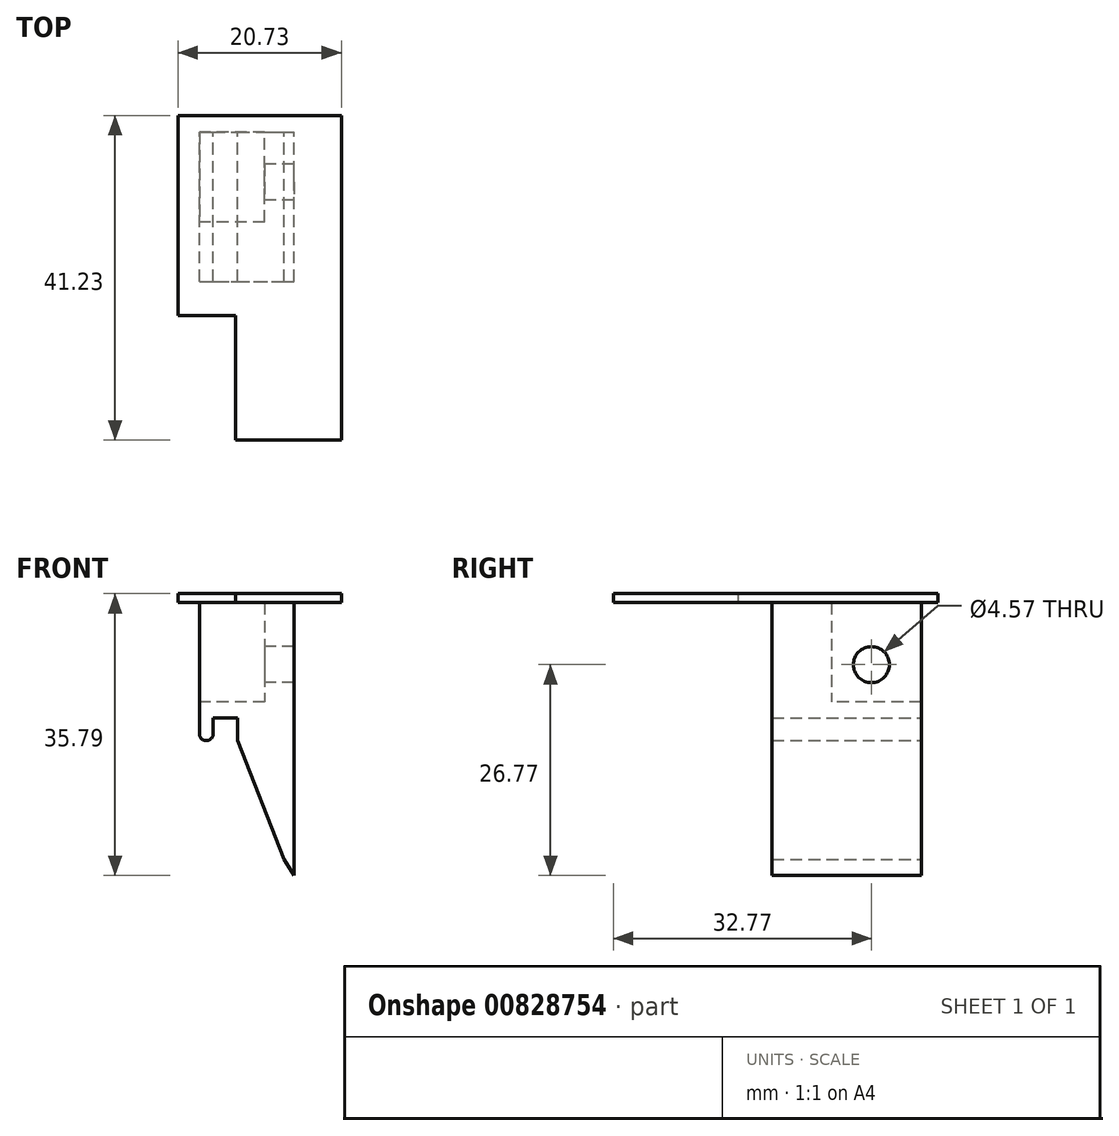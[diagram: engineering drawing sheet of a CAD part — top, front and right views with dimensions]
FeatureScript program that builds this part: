
annotation { "Feature Type Name" : "Feature", "Feature Type Description" : "" }
export const myFeature = defineFeature(function(context is Context, id is Id, definition is map)
    precondition{}
    {
        {
            var Q0;
            Q0=qCreatedBy(makeId("Front.planeOp"),FACE);
            var sketch = newSketch(context, id + "F0", { "sketchPlane" : qUnion([Q0])});
            skLineSegment(sketch, "E0", {"start": v(-12.01, 26.3) * mm, "end": v(-12.01, 8.78) * mm});
            skLineSegment(sketch, "E1", {"start": v(-12.01, 8.78) * mm, "end": v(-10.26, 8.78) * mm});
            skLineSegment(sketch, "E2", {"start": v(-10.26, 8.78) * mm, "end": v(-10.26, 11.67) * mm});
            skLineSegment(sketch, "E3", {"start": v(-10.26, 11.67) * mm, "end": v(-7.14, 11.67) * mm});
            skLineSegment(sketch, "E4", {"start": v(-7.14, 11.67) * mm, "end": v(-7.14, 8.78) * mm});
            skLineSegment(sketch, "E5", {"start": v(-12.01, 26.3) * mm, "end": v(0, 26.3) * mm});
            skLineSegment(sketch, "E6", {"start": v(0, 26.3) * mm, "end": v(0, -8.34) * mm});
            skLineSegment(sketch, "E7", {"start": v(-7.14, 8.78) * mm, "end": v(-1.25, -6.3) * mm});
            skLineSegment(sketch, "E8", {"start": v(-1.25, -6.3) * mm, "end": v(0, -8.34) * mm});
            skSolve(sketch);
        }
        {
            var Q0;
            Q0=makeQuery(id+"F0.imprint","IMPRINT",FACE,{"disambiguationData":[TD([[makeQuery(id+"F0.imprint","IMPRINT",EDGE,{"derivedFrom":sQuery(id+"F0.wireOp",EDGE,"E0")}),1.0]])]});
            extrude(context, id + "F1", {"entities" : qUnion([Q0]), "depth" : 18.95 * mm, "offsetDistance" : 25.4 * mm});
        }
        {
            var Q0;
            Q0=makeQuery(id+"F1.opExtrude","SWEPT_FACE",FACE,{"disambiguationData":[OSD([sQuery(id+"F0.wireOp",EDGE,"E5")])]});
            var sketch = newSketch(context, id + "F2", { "sketchPlane" : qUnion([Q0])});
            skLineSegment(sketch, "E9", {"start": v(-14.7, 2.1) * mm, "end": v(6.02, 2.1) * mm});
            skLineSegment(sketch, "E10", {"start": v(6.02, 2.1) * mm, "end": v(6.02, -39.12) * mm});
            skLineSegment(sketch, "E11", {"start": v(6.02, -39.12) * mm, "end": v(-7.41, -39.12) * mm});
            skLineSegment(sketch, "E12", {"start": v(-7.41, -39.12) * mm, "end": v(-7.41, -23.3) * mm});
            skLineSegment(sketch, "E13", {"start": v(-7.41, -23.3) * mm, "end": v(-14.7, -23.3) * mm});
            skLineSegment(sketch, "E14", {"start": v(-14.7, -23.3) * mm, "end": v(-14.7, 2.1) * mm});
            skSolve(sketch);
        }
        {
            var Q0;
            Q0=qSketchRegion(id+"F2",true);
            extrude(context, id + "F3", {"entities" : qUnion([Q0]), "operationType" : NewBodyOperationType.ADD, "depth" : 1.14 * mm, "offsetDistance" : 25.4 * mm});
        }
        {
            var Q0;
            Q0=makeQuery(id+"F1.opExtrude","SWEPT_EDGE",EDGE,{"disambiguationData":[OSD([sQuery(id+"F0.wireOp",EDGE,"E0"),sQuery(id+"F0.wireOp",EDGE,"E1")])]});
            var Q1;
            Q1=makeQuery(id+"F1.opExtrude","SWEPT_EDGE",EDGE,{"disambiguationData":[OSD([sQuery(id+"F0.wireOp",EDGE,"E1"),sQuery(id+"F0.wireOp",EDGE,"E2")])]});
            fillet(context, id + "F4", {"entities" : qUnion([Q0, Q1]), "radius" : 0.84 * mm, "tangentPropagation" : true, "allowEdgeOverflow" : false});
        }
        {
            var Q0;
            Q0=makeQuery(id+"F1.opExtrude","SWEPT_FACE",FACE,{"disambiguationData":[OSD([sQuery(id+"F0.wireOp",EDGE,"E0")])]});
            var sketch = newSketch(context, id + "F5", { "sketchPlane" : qUnion([Q0])});
            skLineSegment(sketch, "E15.bottom", {"start": v(0, 26.3) * mm, "end": v(11.43, 26.3) * mm});
            skLineSegment(sketch, "E15.top", {"start": v(0, 13.7) * mm, "end": v(11.43, 13.7) * mm});
            skLineSegment(sketch, "E15.left", {"start": v(0, 26.3) * mm, "end": v(0, 13.7) * mm});
            skLineSegment(sketch, "E15.right", {"start": v(11.43, 26.3) * mm, "end": v(11.43, 13.7) * mm});
            skPoint(sketch, "E16", {"position": v(6.17, 18.35) * mm});
            skSolve(sketch);
        }
        {
            var Q0;
            Q0=qSketchRegion(id+"F5",true);
            extrude(context, id + "F6", {"entities" : qUnion([Q0]), "operationType" : NewBodyOperationType.REMOVE, "oppositeDirection" : true, "depth" : 8.3 * mm, "offsetDistance" : 25.4 * mm});
        }
        {
            var Q0;
            Q0=makeQuery(id+"F6.boolean.opBoolean","COPY",FACE,{"derivedFrom":makeQuery(id+"F6.opExtrude","CAP_FACE",FACE,{"disambiguationData":[OSD([sQuery(id+"F5.wireOp",EDGE,"E15.bottom"),sQuery(id+"F5.wireOp",EDGE,"E15.top"),sQuery(id+"F5.wireOp",EDGE,"E15.left"),sQuery(id+"F5.wireOp",EDGE,"E15.right")])],"isStart":false})});
            var sketch = newSketch(context, id + "F7", { "sketchPlane" : qUnion([Q0])});
            skLineSegment(sketch, "E17.bottom", {"start": v(0, 26.3) * mm, "end": v(11.43, 26.3) * mm});
            skLineSegment(sketch, "E17.top", {"start": v(0, 13.7) * mm, "end": v(11.43, 13.7) * mm});
            skLineSegment(sketch, "E17.left", {"start": v(0, 26.3) * mm, "end": v(0, 13.7) * mm});
            skLineSegment(sketch, "E17.right", {"start": v(11.43, 26.3) * mm, "end": v(11.43, 13.7) * mm});
            skPoint(sketch, "E18", {"position": v(6.35, 18.43) * mm});
            skSolve(sketch);
        }
        {
            var Q0;
            Q0=sQuery(id+"F7.wireOp",VERTEX,"E18");
            var Q1;
            Q1=makeQuery(id+"F1.opExtrude","SWEPT_BODY",BODY,{"disambiguationData":[OSD([sQuery(id+"F0.wireOp",EDGE,"E0"),sQuery(id+"F0.wireOp",EDGE,"E1"),sQuery(id+"F0.wireOp",EDGE,"E2"),sQuery(id+"F0.wireOp",EDGE,"E3"),sQuery(id+"F0.wireOp",EDGE,"E4"),sQuery(id+"F0.wireOp",EDGE,"E5"),sQuery(id+"F0.wireOp",EDGE,"E6"),sQuery(id+"F0.wireOp",EDGE,"E7"),sQuery(id+"F0.wireOp",EDGE,"E8")])]});
            hole(context, id + "F8", {"style" : HoleStyle.SIMPLE, "endStyle" : HoleEndStyle.THROUGH, "holeDiameter" : 4.57 * mm, "majorDiameter" : 6.35 * mm, "isTappedThrough" : true, "tappedDepth" : 12.7 * mm, "tapClearance" : 3, "locations" : qUnion([Q0]), "scope" : qUnion([Q1])});
        }
    });
